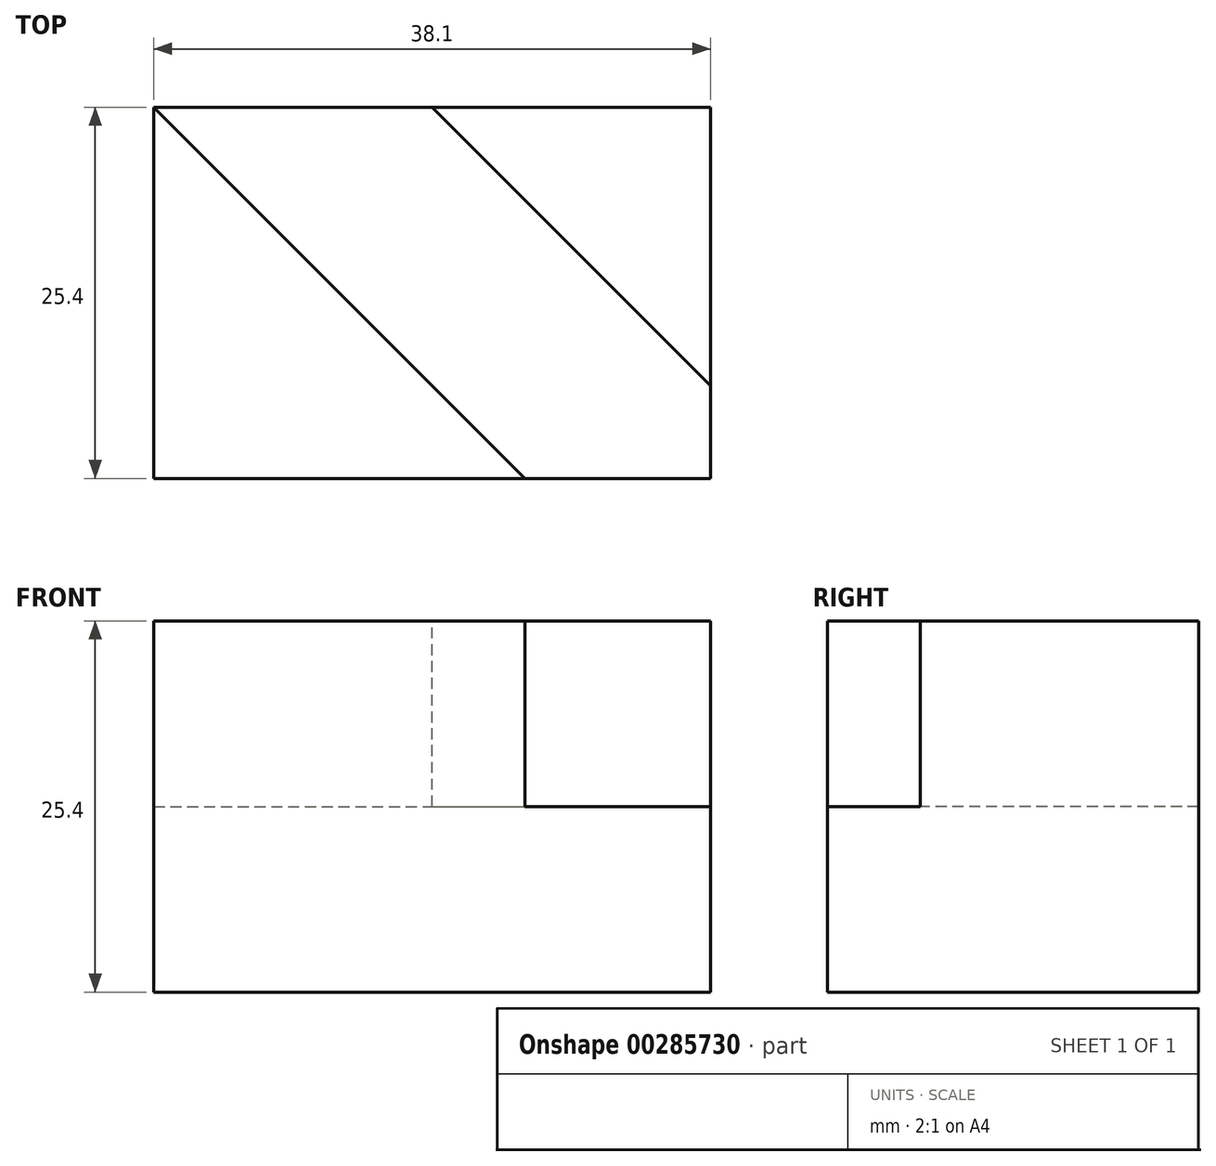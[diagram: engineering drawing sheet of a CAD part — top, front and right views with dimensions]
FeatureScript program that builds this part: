
annotation { "Feature Type Name" : "Feature", "Feature Type Description" : "" }
export const myFeature = defineFeature(function(context is Context, id is Id, definition is map)
    precondition{}
    {
        {
            var Q0;
            Q0=qCreatedBy(makeId("Top.planeOp"),FACE);
            var sketch = newSketch(context, id + "F0", { "sketchPlane" : qUnion([Q0])});
            skLineSegment(sketch, "E0.bottom", {"start": v(0, 0) * mm, "end": v(38.1, 0) * mm});
            skLineSegment(sketch, "E0.top", {"start": v(0, 25.4) * mm, "end": v(38.1, 25.4) * mm});
            skLineSegment(sketch, "E0.left", {"start": v(0, 0) * mm, "end": v(0, 25.4) * mm});
            skLineSegment(sketch, "E0.right", {"start": v(38.1, 0) * mm, "end": v(38.1, 25.4) * mm});
            skLineSegment(sketch, "E1", {"start": v(0, 25.4) * mm, "end": v(25.4, 0) * mm});
            skLineSegment(sketch, "E2", {"start": v(19.05, 25.4) * mm, "end": v(38.1, 6.35) * mm});
            skSolve(sketch);
        }
        {
            var Q0;
            Q0 = qSketchRegion(id + "F0", true);
            extrude(context, id + "F1", {"entities" : qUnion([Q0]), "oppositeDirection" : true, "depth" : 25.4 * mm});
        }
        {
            var Q0;
            {var subQ4=sQuery(id+"F0.wireOp",EDGE,"E1");Q0=makeQuery(id+"F0.imprint","IMPRINT",FACE,{"disambiguationData":[TD([[makeQuery(id+"F0.imprint","IMPRINT",EDGE,{"derivedFrom":subQ4}),1.0]])]});}
            extrude(context, id + "F2", {"entities" : qUnion([Q0]), "operationType" : NewBodyOperationType.REMOVE, "oppositeDirection" : true, "depth" : 12.7 * mm});
        }
    });
